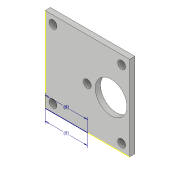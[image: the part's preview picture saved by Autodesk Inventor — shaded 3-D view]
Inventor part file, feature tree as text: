
AUTODESK INVENTOR PART (.ipt)
format: ipt  version: 2019 (Build 230136000, 136)  size: 126,464 bytes
history: native  units: in
note: dims shown in document units (in); Inventor stores cm internally (conversion verified against a paired STEP export)
features: sketch x5, extrude x4
ambient origin geometry x8: Origin, YZ Plane, XZ Plane, XY Plane, X Axis, Y Axis, Z Axis, Center Point
bodies: Solid1 (feature_tree)
feature tree (9):
  extrude  "Extrusion1"  Depth=6.2992in
  extrude  "Extrusion2"  Depth=0.3937in
  sketch  "Sketch3"  dims[d5=0.5906in d6=0.5906in]
  extrude  "Extrusion3"  Depth=0.5906in
  extrude  "Extrusion4"  Depth=0.5906in
  sketch  "Sketch1"  dims[d0=6.2992in d1=6.2992in]
  sketch  "Sketch2"  dims[d2=0.3937in d3=0.0in d4=0.5906in]
  sketch  "Sketch4"  dims[d7=0.5906in d8=0.5906in]
  sketch  "Sketch5"  dims[d9=0.6496in d10=0.5906in d11=0.5906in d12=0.5906in d13=0.5906in d14=0.5906in d15=0.5906in d16=0.3937in d17=0.0in d18=3.1496in d19=3.1496in d20=3.1496in d21=3.1496in d22=3.1496in d23=0.5906in d24=0.3937in d25=0.0in d26=3.1496in d27=1.378in d28=2.3622in d29=0.3937in d30=0.0in]
